# Revit family: Faucet-Wall_Mount-Lavatory-KOHLER-Triton_Bowe_Cannock-K-730T70
name_source: partatom
category: Plumbing Fixtures
units: mm (PartAtom-declared; Revit-internal decimal feet)

## family parameters
Cut with Voids When Loaded = No
Host = Face
OmniClass Number = 23.31.11.00
Part Type = Normal
Room Calculation Point = No
Round Connector Dimension = Use Diameter
Shared = No

## types (1)
- Service sink faucet, CP-Polished Chrome
    ADA Compliant = Yes
    Assembly Code = D2010
    CW Connection = Yes
    Cold Water Inlet = Cold Water Inlet
    Date Modified = 06/26/2019
    Default Elevation = 36"
    Description = Full-flow service sink faucet with 3-11/16 inch gooseneck spout and lever handles
    Drain Included = No
    Edition number = 1
    Faucet Hole Spacing = 3"
    Finish = Kohler-Metal-CP-Polished_Chrome
    Flow Rate = 1 GPM
    HW Connection = Yes
    Handle Clearance = 2 7/16"
    Height = 11 1/8"
    Hot Water Inlet = Hot Water Inlet
    Length = 7 5/16"
    Manufacturer = KOHLER Co.
    MasterFormat 1995 = 15410
    MasterFormat 2004 = 22.41.39
    Material = Brass Construction
    Model = K-730T70-4AR-CP
    Pressure = 60.00 psi
    Product Documentation Link = https://www.us.kohler.com
    Product Guid = 7c7f995b-fe48-4606-a90d-fd27283239f2
    Product Name = Triton Bowe Cannock
    Product Page URL = http://www.us.kohler.com
    Product data url = https://bimobject.com
    Spout Reach = 3 11/16"
    Type = 1
    URL = https://www.us.kohler.com
    Vent Connection = No
    Waste Connection = No
    Waste Water Outlet = Waste Water Outlet
    WaterSense Certified = Yes
    Width = 7 3/8"

## geometry (parser evidence)
native form markers: Sweep x6
no freeform markers — native parametric forms only
